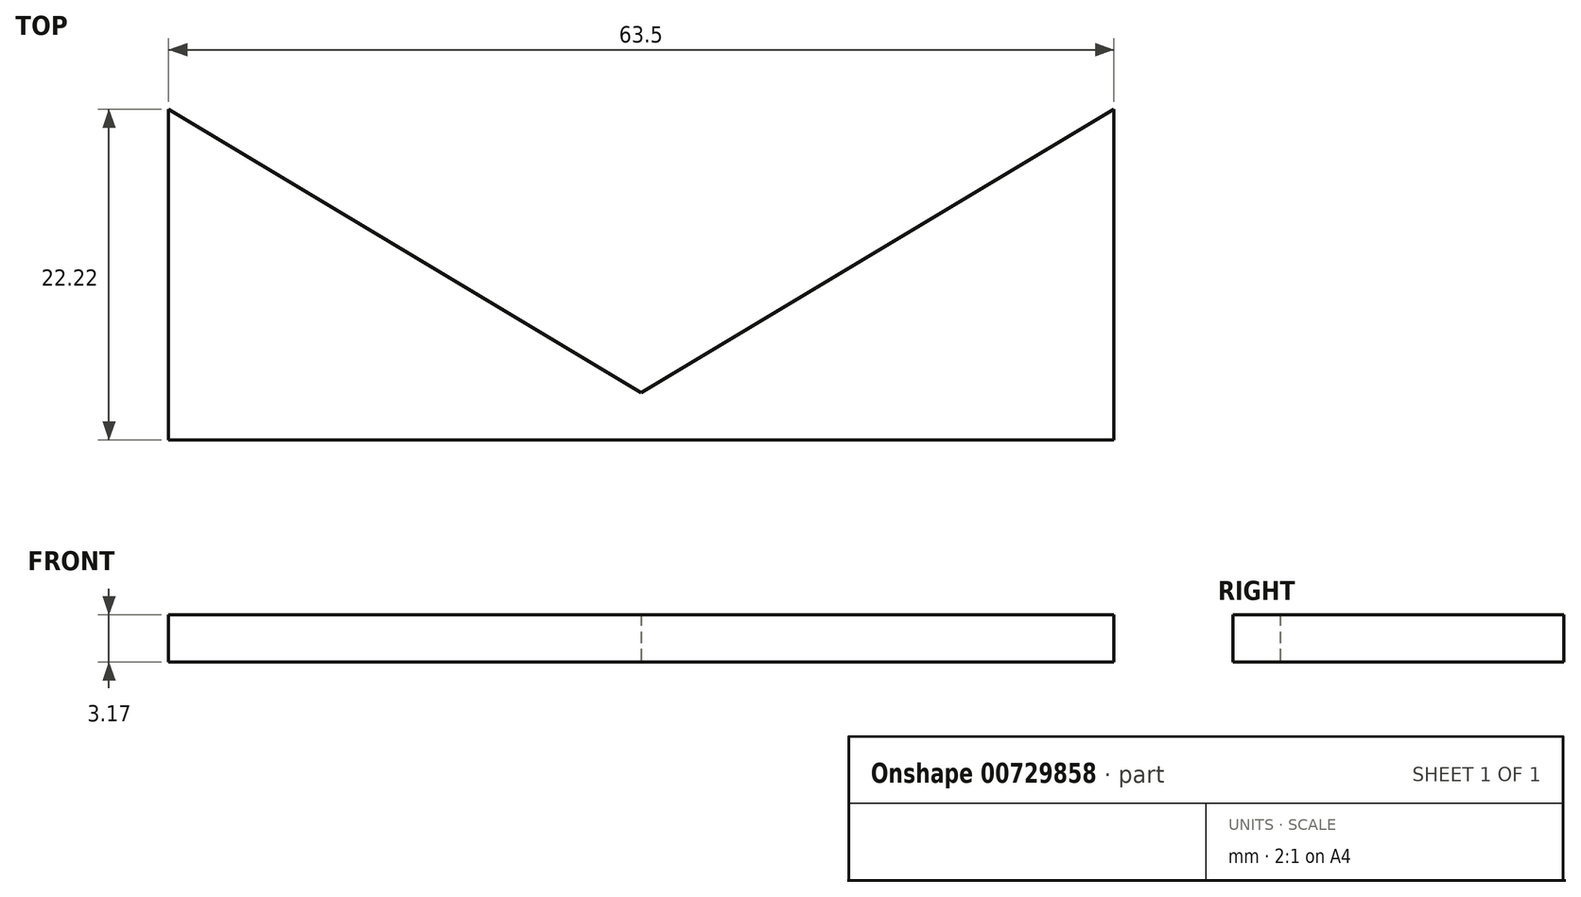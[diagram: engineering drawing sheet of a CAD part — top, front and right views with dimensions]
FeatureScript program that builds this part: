
annotation { "Feature Type Name" : "Feature", "Feature Type Description" : "" }
export const myFeature = defineFeature(function(context is Context, id is Id, definition is map)
    precondition{}
    {
        {
            var Q0;
            Q0=qCreatedBy(makeId("Top.planeOp"),FACE);
            var sketch = newSketch(context, id + "F0", { "sketchPlane" : qUnion([Q0])});
            skLineSegment(sketch, "E0.bottom", {"start": v(0, 6.42) * mm, "end": v(63.5, 6.42) * mm});
            skLineSegment(sketch, "E0.top", {"start": v(0, 9.6) * mm, "end": v(63.5, 9.6) * mm});
            skLineSegment(sketch, "E0.left", {"start": v(0, 6.42) * mm, "end": v(0, 9.6) * mm});
            skLineSegment(sketch, "E0.right", {"start": v(63.5, 6.42) * mm, "end": v(63.5, 9.6) * mm});
            skLineSegment(sketch, "E1", {"start": v(0, 9.6) * mm, "end": v(0, 47.7) * mm});
            skLineSegment(sketch, "E2", {"start": v(0, 47.7) * mm, "end": v(63.5, 9.6) * mm});
            skLineSegment(sketch, "E3", {"start": v(63.5, 9.6) * mm, "end": v(63.5, 47.7) * mm});
            skLineSegment(sketch, "E4", {"start": v(63.5, 47.7) * mm, "end": v(0, 9.6) * mm});
            skLineSegment(sketch, "E5", {"start": v(31.75, 9.6) * mm, "end": v(0, 28.64) * mm});
            skLineSegment(sketch, "E6", {"start": v(31.75, 9.6) * mm, "end": v(63.5, 28.64) * mm});
            skLineSegment(sketch, "E7.bottom", {"start": v(12.7, 6.42) * mm, "end": v(50.8, 6.42) * mm});
            skLineSegment(sketch, "E7.top", {"start": v(12.7, 0.07) * mm, "end": v(50.8, 0.07) * mm});
            skLineSegment(sketch, "E7.left", {"start": v(12.7, 6.42) * mm, "end": v(12.7, 0.07) * mm});
            skLineSegment(sketch, "E7.right", {"start": v(50.8, 6.42) * mm, "end": v(50.8, 0.07) * mm});
            skSolve(sketch);
        }
        {
            var Q0;
            {var subQ1=sQuery(id+"F0.wireOp",EDGE,"E1");var subQ3=sQuery(id+"F0.wireOp",EDGE,"E5");var subQ4=makeQuery(id+"F0.imprint","INTERSECT",VERTEX,{"derivedFrom":[subQ1,subQ3]});Q0=makeQuery(id+"F0.imprint","IMPRINT",FACE,{"disambiguationData":[TD([[makeQuery(id+"F0.imprint","IMPRINT",EDGE,{"disambiguationData":[TD([[subQ4,1.0]])],"derivedFrom":subQ3}),1.0]])]});}
            var Q1;
            {var subQ0=sQuery(id+"F0.wireOp",EDGE,"E4");var subQ3=sQuery(id+"F0.wireOp",EDGE,"E5");var subQ5=makeQuery(id+"F0.imprint","INTERSECT",VERTEX,{"derivedFrom":[subQ0,subQ3]});Q1=makeQuery(id+"F0.imprint","IMPRINT",FACE,{"disambiguationData":[TD([[makeQuery(id+"F0.imprint","IMPRINT",EDGE,{"disambiguationData":[TD([[subQ5,1.0]])],"derivedFrom":subQ3}),1.0]])]});}
            var Q2;
            {var subQ0=sQuery(id+"F0.wireOp",EDGE,"E2");var subQ3=sQuery(id+"F0.wireOp",EDGE,"E6");var subQ5=makeQuery(id+"F0.imprint","INTERSECT",VERTEX,{"derivedFrom":[subQ0,subQ3]});Q2=makeQuery(id+"F0.imprint","IMPRINT",FACE,{"disambiguationData":[TD([[makeQuery(id+"F0.imprint","IMPRINT",EDGE,{"disambiguationData":[TD([[subQ5,1.0]])],"derivedFrom":subQ3}),-1.0]])]});}
            var Q3;
            {var subQ0=sQuery(id+"F0.wireOp",EDGE,"E3");var subQ3=sQuery(id+"F0.wireOp",EDGE,"E6");var subQ5=makeQuery(id+"F0.imprint","INTERSECT",VERTEX,{"derivedFrom":[subQ0,subQ3]});Q3=makeQuery(id+"F0.imprint","IMPRINT",FACE,{"disambiguationData":[TD([[makeQuery(id+"F0.imprint","IMPRINT",EDGE,{"disambiguationData":[TD([[subQ5,1.0]])],"derivedFrom":subQ3}),-1.0]])]});}
            var Q4;
            Q4=makeQuery(id+"F0.imprint","IMPRINT",FACE,{"disambiguationData":[TD([[makeQuery(id+"F0.imprint","IMPRINT",EDGE,{"derivedFrom":sQuery(id+"F0.wireOp",EDGE,"E0.bottom")}),1.0]])]});
            var Q5;
            Q5=makeQuery(id+"F0.imprint","IMPRINT",FACE,{"disambiguationData":[TD([[makeQuery(id+"F0.imprint","IMPRINT",EDGE,{"derivedFrom":sQuery(id+"F0.wireOp",EDGE,"E7.bottom")}),-1.0]])]});
            extrude(context, id + "F1", {"entities" : qUnion([Q0, Q1, Q2, Q3, Q4, Q5]), "depth" : 3.17 * mm, "offsetDistance" : 25.4 * mm});
        }
    });
